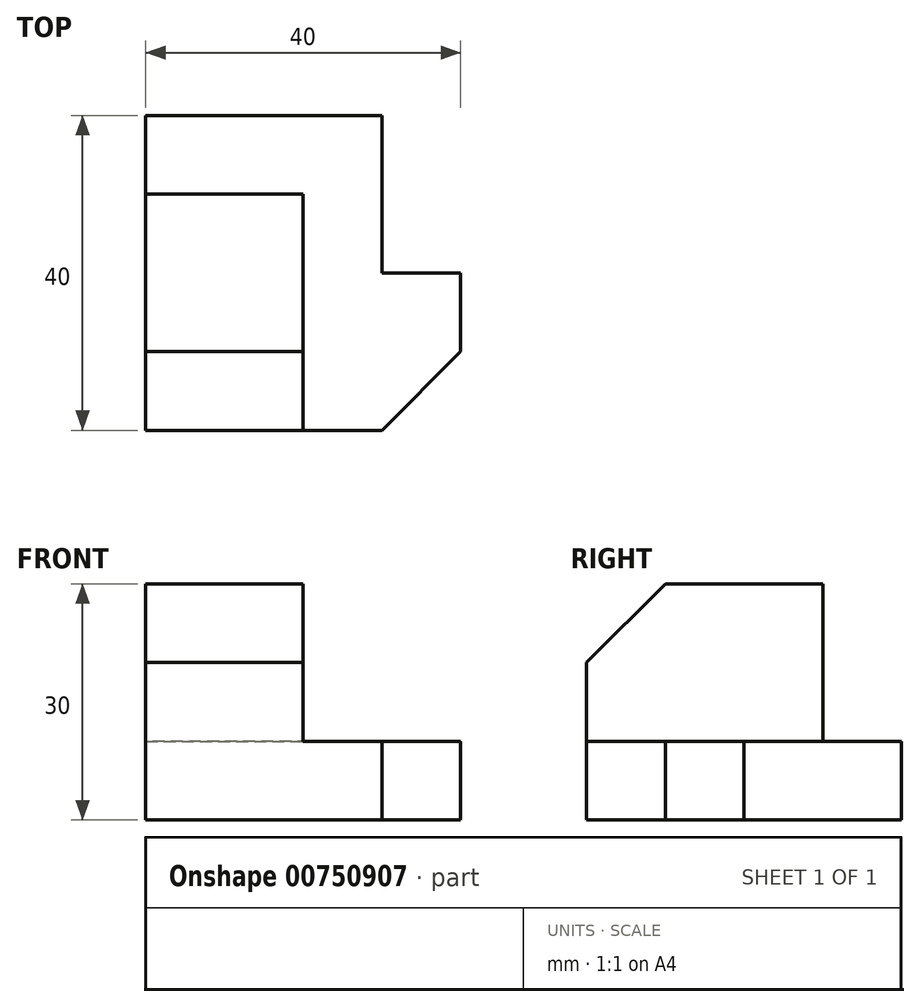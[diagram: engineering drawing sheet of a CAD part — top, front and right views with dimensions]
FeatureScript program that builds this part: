
annotation { "Feature Type Name" : "Feature", "Feature Type Description" : "" }
export const myFeature = defineFeature(function(context is Context, id is Id, definition is map)
    precondition{}
    {
        {
            var Q0;
            Q0=qCreatedBy(makeId("Front.planeOp"),FACE);
            var sketch = newSketch(context, id + "F0", { "sketchPlane" : qUnion([Q0])});
            skLineSegment(sketch, "E0", {"start": v(0, 0) * mm, "end": v(40, 0) * mm});
            skLineSegment(sketch, "E1", {"start": v(40, 0) * mm, "end": v(40, 10) * mm});
            skLineSegment(sketch, "E2", {"start": v(40, 10) * mm, "end": v(20, 10) * mm});
            skLineSegment(sketch, "E3", {"start": v(20, 10) * mm, "end": v(20, 30) * mm});
            skLineSegment(sketch, "E4", {"start": v(20, 30) * mm, "end": v(0, 30) * mm});
            skLineSegment(sketch, "E5", {"start": v(0, 30) * mm, "end": v(0, 0) * mm});
            skSolve(sketch);
        }
        {
            var Q0;
            Q0=makeQuery(id+"F0.imprint","IMPRINT",FACE,{"disambiguationData":[TD([[makeQuery(id+"F0.imprint","IMPRINT",EDGE,{"derivedFrom":sQuery(id+"F0.wireOp",EDGE,"E0")}),1.0]])]});
            extrude(context, id + "F1", {"entities" : qUnion([Q0]), "depth" : 40 * mm, "offsetDistance" : 25 * mm});
        }
        {
            var Q0;
            Q0=makeQuery(id+"F1.opExtrude","SWEPT_FACE",FACE,{"disambiguationData":[OSD([sQuery(id+"F0.wireOp",EDGE,"E3")])]});
            var sketch = newSketch(context, id + "F2", { "sketchPlane" : qUnion([Q0])});
            skLineSegment(sketch, "E6", {"start": v(0, 30) * mm, "end": v(-10, 30) * mm});
            skLineSegment(sketch, "E7", {"start": v(-10, 30) * mm, "end": v(-10, 10) * mm});
            skLineSegment(sketch, "E8", {"start": v(-10, 10) * mm, "end": v(0, 10) * mm});
            skLineSegment(sketch, "E9", {"start": v(0, 10) * mm, "end": v(0, 30) * mm});
            skSolve(sketch);
        }
        {
            var Q0;
            Q0=makeQuery(id+"F2.imprint","IMPRINT",FACE,{"disambiguationData":[TD([[makeQuery(id+"F2.imprint","IMPRINT",EDGE,{"derivedFrom":sQuery(id+"F2.wireOp",EDGE,"E6")}),-1.0]])]});
            extrude(context, id + "F3", {"entities" : qUnion([Q0]), "operationType" : NewBodyOperationType.REMOVE, "oppositeDirection" : true, "depth" : 20 * mm, "offsetDistance" : 25 * mm});
        }
        {
            var Q0;
            Q0=makeQuery(id+"F3.boolean.opBoolean","MERGE",FACE,{"derivedFrom":[makeQuery(id+"F1.opExtrude","SWEPT_FACE",FACE,{"disambiguationData":[OSD([sQuery(id+"F0.wireOp",EDGE,"E2")])]}),makeQuery(id+"F3.opExtrude","SWEPT_FACE",FACE,{"disambiguationData":[OSD([sQuery(id+"F2.wireOp",EDGE,"E8")])]})]});
            var sketch = newSketch(context, id + "F4", { "sketchPlane" : qUnion([Q0])});
            skLineSegment(sketch, "E10", {"start": v(40, 0) * mm, "end": v(30, 0) * mm});
            skLineSegment(sketch, "E11", {"start": v(30, 0) * mm, "end": v(30, -20) * mm});
            skLineSegment(sketch, "E12", {"start": v(30, -20) * mm, "end": v(40, -20) * mm});
            skLineSegment(sketch, "E13", {"start": v(40, -20) * mm, "end": v(40, 0) * mm});
            skSolve(sketch);
        }
        {
            var Q0;
            Q0=makeQuery(id+"F4.imprint","IMPRINT",FACE,{"disambiguationData":[TD([[makeQuery(id+"F4.imprint","IMPRINT",EDGE,{"derivedFrom":sQuery(id+"F4.wireOp",EDGE,"E10")}),1.0]])]});
            extrude(context, id + "F5", {"entities" : qUnion([Q0]), "operationType" : NewBodyOperationType.REMOVE, "oppositeDirection" : true, "depth" : 10 * mm, "offsetDistance" : 25 * mm});
        }
        {
            var Q0;
            Q0=makeQuery(id+"F3.boolean.opBoolean","MERGE",FACE,{"derivedFrom":[makeQuery(id+"F1.opExtrude","SWEPT_FACE",FACE,{"disambiguationData":[OSD([sQuery(id+"F0.wireOp",EDGE,"E2")])]}),makeQuery(id+"F3.opExtrude","SWEPT_FACE",FACE,{"disambiguationData":[OSD([sQuery(id+"F2.wireOp",EDGE,"E8")])]})]});
            var sketch = newSketch(context, id + "F6", { "sketchPlane" : qUnion([Q0])});
            skLineSegment(sketch, "E14", {"start": v(30, -40) * mm, "end": v(40, -30) * mm});
            skLineSegment(sketch, "E15", {"start": v(40, -30) * mm, "end": v(40, -40) * mm});
            skLineSegment(sketch, "E16", {"start": v(40, -40) * mm, "end": v(30, -40) * mm});
            skSolve(sketch);
        }
        {
            var Q0;
            Q0=makeQuery(id+"F6.imprint","IMPRINT",FACE,{"disambiguationData":[TD([[makeQuery(id+"F6.imprint","IMPRINT",EDGE,{"derivedFrom":sQuery(id+"F6.wireOp",EDGE,"E14")}),-1.0]])]});
            extrude(context, id + "F7", {"entities" : qUnion([Q0]), "operationType" : NewBodyOperationType.REMOVE, "oppositeDirection" : true, "depth" : 10 * mm, "offsetDistance" : 25 * mm});
        }
        {
            var Q0;
            Q0=makeQuery(id+"F1.opExtrude","SWEPT_FACE",FACE,{"disambiguationData":[OSD([sQuery(id+"F0.wireOp",EDGE,"E3")])]});
            var sketch = newSketch(context, id + "F8", { "sketchPlane" : qUnion([Q0])});
            skLineSegment(sketch, "E17", {"start": v(-40, 20) * mm, "end": v(-30, 30) * mm});
            skLineSegment(sketch, "E18", {"start": v(-30, 30) * mm, "end": v(-40, 30) * mm});
            skLineSegment(sketch, "E19", {"start": v(-40, 30) * mm, "end": v(-40, 20) * mm});
            skSolve(sketch);
        }
        {
            var Q0;
            Q0=makeQuery(id+"F8.imprint","IMPRINT",FACE,{"disambiguationData":[TD([[makeQuery(id+"F8.imprint","IMPRINT",EDGE,{"derivedFrom":sQuery(id+"F8.wireOp",EDGE,"E17")}),1.0]])]});
            extrude(context, id + "F9", {"entities" : qUnion([Q0]), "operationType" : NewBodyOperationType.REMOVE, "oppositeDirection" : true, "depth" : 20 * mm, "offsetDistance" : 25 * mm});
        }
    });
